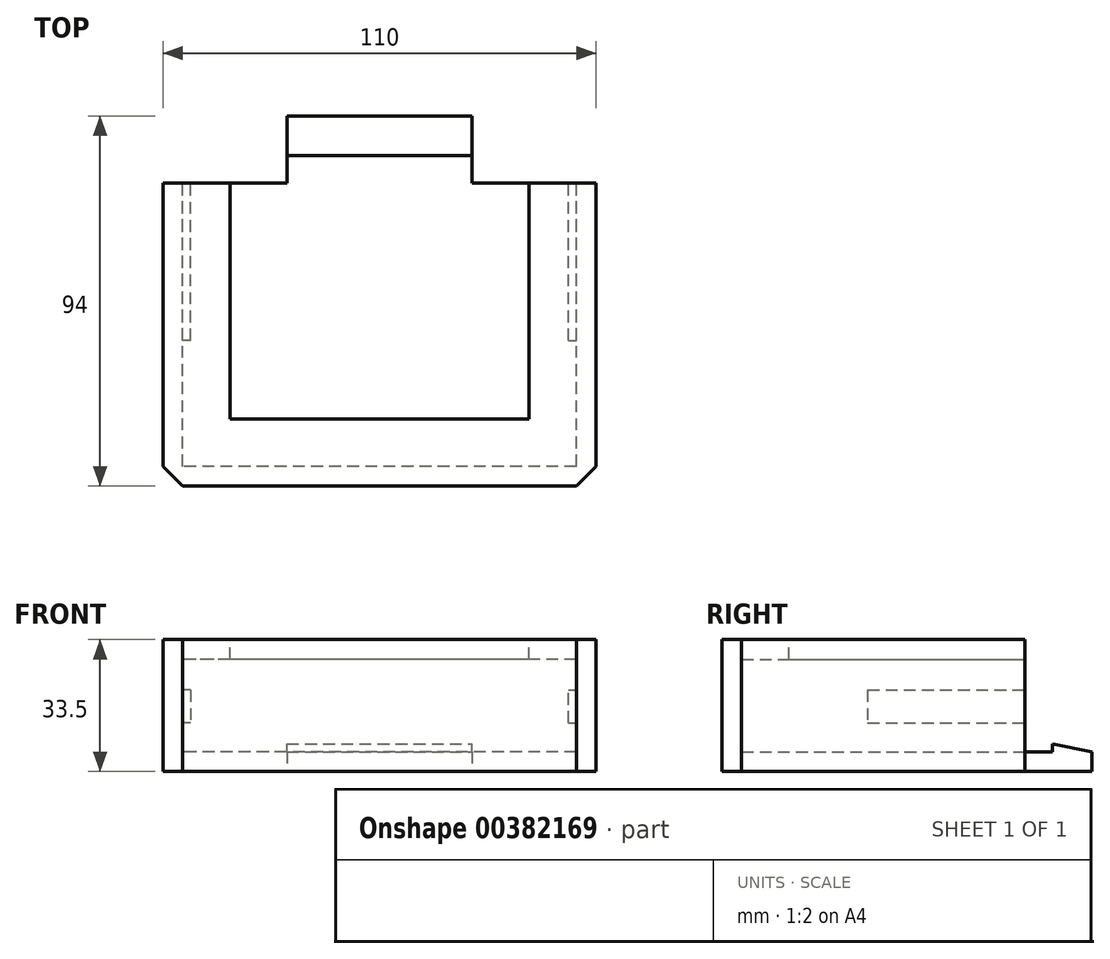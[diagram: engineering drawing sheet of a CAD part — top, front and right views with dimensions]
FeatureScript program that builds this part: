
annotation { "Feature Type Name" : "Feature", "Feature Type Description" : "" }
export const myFeature = defineFeature(function(context is Context, id is Id, definition is map)
    precondition{}
    {
        {
            var Q0;
            Q0=qCreatedBy(makeId("Top.planeOp"),FACE);
            var sketch = newSketch(context, id + "F0", { "sketchPlane" : qUnion([Q0])});
            skLineSegment(sketch, "E0.bottom", {"start": v(-55, 38.5) * mm, "end": v(55, 38.5) * mm});
            skLineSegment(sketch, "E0.top", {"start": v(-55, -38.5) * mm, "end": v(55, -38.5) * mm});
            skLineSegment(sketch, "E0.left", {"start": v(-55, 38.5) * mm, "end": v(-55, -38.5) * mm});
            skLineSegment(sketch, "E0.right", {"start": v(55, 38.5) * mm, "end": v(55, -38.5) * mm});
            skPoint(sketch, "E0.middle", {"position": v(0, 0) * mm});
            skSolve(sketch);
        }
        {
            var Q0;
            Q0 = qSketchRegion(id + "F0", true);
            extrude(context, id + "F1", {"entities" : qUnion([Q0]), "depth" : 33.5 * mm});
        }
        {
            var Q0;
            Q0=makeQuery(id+"F1.opExtrude","SWEPT_FACE",FACE,{"disambiguationData":[OSD([sQuery(id+"F0.wireOp",EDGE,"E0.bottom")])]});
            var sketch = newSketch(context, id + "F2", { "sketchPlane" : qUnion([Q0])});
            skLineSegment(sketch, "E1.bottom", {"start": v(-50, 28.5) * mm, "end": v(50, 28.5) * mm});
            skLineSegment(sketch, "E1.top", {"start": v(-50, 5) * mm, "end": v(50, 5) * mm});
            skLineSegment(sketch, "E1.left", {"start": v(-50, 28.5) * mm, "end": v(-50, 5) * mm});
            skLineSegment(sketch, "E1.right", {"start": v(50, 28.5) * mm, "end": v(50, 5) * mm});
            skSolve(sketch);
        }
        {
            var Q0;
            Q0=makeQuery(id+"F2.imprint","IMPRINT",FACE,{"disambiguationData":[TD([[makeQuery(id+"F2.imprint","IMPRINT",EDGE,{"derivedFrom":sQuery(id+"F2.wireOp",EDGE,"E1.bottom")}),-1.0]])]});
            var sketch = newSketch(context, id + "F3", { "sketchPlane" : qUnion([Q0])});
            skLineSegment(sketch, "E2.bottom", {"start": v(48, 20.67) * mm, "end": v(50, 20.67) * mm});
            skLineSegment(sketch, "E2.top", {"start": v(48, 12.33) * mm, "end": v(50, 12.33) * mm});
            skLineSegment(sketch, "E2.left", {"start": v(48, 20.67) * mm, "end": v(48, 12.33) * mm});
            skLineSegment(sketch, "E2.right", {"start": v(50, 20.67) * mm, "end": v(50, 12.33) * mm});
            skPoint(sketch, "E2.middle", {"position": v(49, 16.5) * mm});
            skLineSegment(sketch, "E3.bottom", {"start": v(-48, 12.33) * mm, "end": v(-50, 12.33) * mm});
            skLineSegment(sketch, "E3.top", {"start": v(-48, 20.66) * mm, "end": v(-50, 20.66) * mm});
            skLineSegment(sketch, "E3.left", {"start": v(-48, 12.33) * mm, "end": v(-48, 20.67) * mm});
            skLineSegment(sketch, "E3.right", {"start": v(-50, 12.33) * mm, "end": v(-50, 20.67) * mm});
            skPoint(sketch, "E3.middle", {"position": v(-49, 16.5) * mm});
            skSolve(sketch);
        }
        {
            var Q0;
            Q0 = qSketchRegion(id + "F2", true);
            extrude(context, id + "F4", {"entities" : qUnion([Q0]), "operationType" : NewBodyOperationType.REMOVE, "oppositeDirection" : true, "depth" : 72 * mm});
        }
        {
            var Q0;
            Q0 = qSketchRegion(id + "F3", true);
            extrude(context, id + "F5", {"entities" : qUnion([Q0]), "operationType" : NewBodyOperationType.ADD, "oppositeDirection" : true, "depth" : 40 * mm});
        }
        {
            var Q0;
            Q0=makeQuery(id+"F1.opExtrude","CAP_FACE",FACE,{"disambiguationData":[OSD([sQuery(id+"F0.wireOp",EDGE,"E0.bottom"),sQuery(id+"F0.wireOp",EDGE,"E0.top"),sQuery(id+"F0.wireOp",EDGE,"E0.left"),sQuery(id+"F0.wireOp",EDGE,"E0.right")])],"isStart":false});
            var sketch = newSketch(context, id + "F6", { "sketchPlane" : qUnion([Q0])});
            skLineSegment(sketch, "E4.bottom", {"start": v(-38, 38.5) * mm, "end": v(38, 38.5) * mm});
            skLineSegment(sketch, "E4.top", {"start": v(-38, -21.5) * mm, "end": v(38, -21.5) * mm});
            skLineSegment(sketch, "E4.left", {"start": v(-38, 38.5) * mm, "end": v(-38, -21.5) * mm});
            skLineSegment(sketch, "E4.right", {"start": v(38, 38.5) * mm, "end": v(38, -21.5) * mm});
            skSolve(sketch);
        }
        {
            var Q0;
            Q0 = qSketchRegion(id + "F6", true);
            extrude(context, id + "F7", {"entities" : qUnion([Q0]), "operationType" : NewBodyOperationType.REMOVE, "oppositeDirection" : true, "depth" : 20.9 * mm});
        }
        {
            var Q0;
            Q0=makeQuery(id+"F5.boolean.opBoolean","MERGE",FACE,{"derivedFrom":[makeQuery(id+"F1.opExtrude","SWEPT_FACE",FACE,{"disambiguationData":[OSD([sQuery(id+"F0.wireOp",EDGE,"E0.bottom")])]}),makeQuery(id+"F5.opExtrude","CAP_FACE",FACE,{"disambiguationData":[OSD([sQuery(id+"F3.wireOp",EDGE,"E2.bottom"),sQuery(id+"F3.wireOp",EDGE,"E2.top"),sQuery(id+"F3.wireOp",EDGE,"E2.left"),sQuery(id+"F3.wireOp",EDGE,"E2.right")])],"isStart":true}),makeQuery(id+"F5.opExtrude","CAP_FACE",FACE,{"disambiguationData":[OSD([sQuery(id+"F3.wireOp",EDGE,"E3.bottom"),sQuery(id+"F3.wireOp",EDGE,"E3.top"),sQuery(id+"F3.wireOp",EDGE,"E3.left"),sQuery(id+"F3.wireOp",EDGE,"E3.right")])],"isStart":true})]});
            var sketch = newSketch(context, id + "F8", { "sketchPlane" : qUnion([Q0])});
            skLineSegment(sketch, "E5.bottom", {"start": v(-23.5, 5) * mm, "end": v(23.5, 5) * mm});
            skLineSegment(sketch, "E5.top", {"start": v(-23.5, 0) * mm, "end": v(23.5, 0) * mm});
            skLineSegment(sketch, "E5.left", {"start": v(-23.5, 5) * mm, "end": v(-23.5, 0) * mm});
            skLineSegment(sketch, "E5.right", {"start": v(23.5, 5) * mm, "end": v(23.5, 0) * mm});
            skPoint(sketch, "E5.middle", {"position": v(0, 2.5) * mm});
            skSolve(sketch);
        }
        {
            var Q0;
            Q0 = qSketchRegion(id + "F8", true);
            extrude(context, id + "F9", {"entities" : qUnion([Q0]), "operationType" : NewBodyOperationType.ADD, "depth" : 17 * mm});
        }
        {
            var Q0;
            Q0=makeQuery(id+"F9.boolean.opBoolean","MERGE",FACE,{"derivedFrom":[makeQuery(id+"F4.boolean.opBoolean","COPY",FACE,{"derivedFrom":makeQuery(id+"F4.opExtrude","SWEPT_FACE",FACE,{"disambiguationData":[OSD([sQuery(id+"F2.wireOp",EDGE,"E1.top")])]})}),makeQuery(id+"F9.opExtrude","SWEPT_FACE",FACE,{"disambiguationData":[OSD([sQuery(id+"F8.wireOp",EDGE,"E5.bottom")])]})]});
            var sketch = newSketch(context, id + "F10", { "sketchPlane" : qUnion([Q0])});
            skPoint(sketch, "E6", {"position": v(23.5, 45.5) * mm});
            skPoint(sketch, "E7", {"position": v(-23.5, 45.5) * mm});
            skLineSegment(sketch, "E8.bottom", {"start": v(-23.5, 45.5) * mm, "end": v(23.5, 45.5) * mm});
            skLineSegment(sketch, "E8.top", {"start": v(-23.5, 55.5) * mm, "end": v(23.5, 55.5) * mm});
            skLineSegment(sketch, "E8.left", {"start": v(-23.5, 45.5) * mm, "end": v(-23.5, 55.5) * mm});
            skLineSegment(sketch, "E8.right", {"start": v(23.5, 45.5) * mm, "end": v(23.5, 55.5) * mm});
            skSolve(sketch);
        }
        {
            var Q0;
            Q0 = qSketchRegion(id + "F10", true);
            extrude(context, id + "F11", {"entities" : qUnion([Q0]), "operationType" : NewBodyOperationType.ADD, "depth" : 2 * mm});
        }
        {
            var Q0;
            Q0=makeQuery(id+"F11.boolean.opBoolean","MERGE",FACE,{"derivedFrom":[makeQuery(id+"F9.opExtrude","SWEPT_FACE",FACE,{"disambiguationData":[OSD([sQuery(id+"F8.wireOp",EDGE,"E5.right")])]}),makeQuery(id+"F11.opExtrude","SWEPT_FACE",FACE,{"disambiguationData":[OSD([sQuery(id+"F10.wireOp",EDGE,"E8.left")])]})]});
            var sketch = newSketch(context, id + "F12", { "sketchPlane" : qUnion([Q0])});
            skPoint(sketch, "E9", {"position": v(-55.5, 5) * mm});
            skLineSegment(sketch, "E10", {"start": v(-55.5, 5) * mm, "end": v(-45.5, 7) * mm});
            skLineSegment(sketch, "E11", {"start": v(-45.5, 7) * mm, "end": v(-45.5, 5) * mm});
            skLineSegment(sketch, "E12", {"start": v(-45.5, 5) * mm, "end": v(-55.5, 5) * mm});
            skSolve(sketch);
        }
        {
            var Q0;
            {var subQ0=sQuery(id+"F12.wireOp",EDGE,"E10");Q0=makeQuery(id+"F12.imprint","IMPRINT",FACE,{"disambiguationData":[TD([[makeQuery(id+"F12.imprint","IMPRINT",EDGE,{"derivedFrom":subQ0}),1.0]])]});}
            extrude(context, id + "F13", {"entities" : qUnion([Q0]), "operationType" : NewBodyOperationType.REMOVE, "oppositeDirection" : true, "depth" : 55.8 * mm});
        }
        {
            var Q0;
            Q0=makeQuery(id+"F1.opExtrude","SWEPT_EDGE",EDGE,{"disambiguationData":[OSD([sQuery(id+"F0.wireOp",EDGE,"E0.top"),sQuery(id+"F0.wireOp",EDGE,"E0.right")])]});
            var Q1;
            Q1=makeQuery(id+"F1.opExtrude","SWEPT_EDGE",EDGE,{"disambiguationData":[OSD([sQuery(id+"F0.wireOp",EDGE,"E0.top"),sQuery(id+"F0.wireOp",EDGE,"E0.left")])]});
            chamfer(context, id + "F14", {"entities" : qUnion([Q0, Q1]), "width" : 5 * mm, "tangentPropagation" : true});
        }
    });
